# Revit family: Sanitary_Showers_hansgrohe_26066000-Raindance-Select-S-Showerpipe-2_5
name_source: partatom
category: Plumbing Fixtures
revit_build: Autodesk Revit 2018 (Build: 20170223_1515(x64)
units: mm (PartAtom-declared; Revit-internal decimal feet)

## family parameters
Always vertical = No
Cut with Voids When Loaded = No
OmniClass Number = 23.45.00.00
OmniClass Title = Sanitary, Laundry, and Cleaning Equipment
Part Type = Normal
Room Calculation Point = No
Round Connector Dimension = Use Diameter
Shared = No
Work Plane-Based = Yes

## types (1)
- 000 Chrome
    BIMobject category = Showers
    Default Elevation = 4' - 0"
    Design country = Germany
    EAN code = 4059625275856
    Edition number = 1
    GTIN code = https://4059625275856
    IFC Classification = Sanitary Terminal
    Installation instructions = https://www.hansgrohe.com
    Manufacturer country = Germany
    Manufacturer name = hansgrohe
    Material main = Chrome
    Material secondary = Chrome
    Product Guid = d29bcb1f-e20b-46f0-8565-dd55cffc105e
    Product SKU = 26066000
    Product data url = https://www.bimobject.com
    Product family = Raindance Select S
    Product group = Showerpipes with thermostat
    Product name = 26066000 Raindance Select S Showerpipe 240 1jet PowderRain with thermostat 160cc Sweden
    Product url = https://www.hansgrohe.com
    QR code = https://www.bimobject.com
    Technical description = https://www.hansgrohe.com
    Uniclass 1.4 Code = L7214
    Uniclass 1.4 Description = Showers
    Uniclass 2015 Code = SL_35_80_80
    Uniclass 2015 Name = Showers
    Weight Net (Kg) = 6

## geometry (parser evidence)
native form markers: Sweep x2
no freeform markers — native parametric forms only
